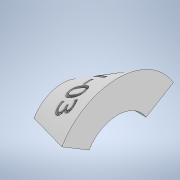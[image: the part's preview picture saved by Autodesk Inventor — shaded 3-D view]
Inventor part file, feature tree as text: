
AUTODESK INVENTOR PART (.ipt)
format: ipt  version: 2021.1 (Build 251245000, 245)  size: 381,952 bytes
history: native  units: in
note: dims shown in document units (in); Inventor stores cm internally (conversion verified against a paired STEP export)
features: sketch x2, revolve x1, plane x1, emboss x1
ambient origin geometry x8: Origin, YZ Plane, XZ Plane, XY Plane, X Axis, Y Axis, Z Axis, Center Point
bodies: Solid1 (feature_tree)
feature tree (5):
  revolve  "Revolution1"  Angle=30.0deg
  plane  "Work Plane5"
  emboss  "Emboss1"
  sketch  "Sketch1"  dims[d1=0.3125in d3=30.0deg]
  sketch  "Sketch4"  dims[d4=0.8108in d7=0.3in d9=0.6125in d11=0.025in d12=0.0in]
